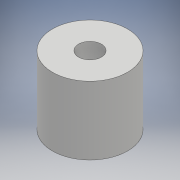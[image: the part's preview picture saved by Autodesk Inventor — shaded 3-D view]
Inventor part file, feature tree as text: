
AUTODESK INVENTOR PART (.ipt)
format: ipt  version: 2018 (Build 220112000, 112)  size: 97,792 bytes
history: native  units: mm
features: extrude x1, sketch x1
ambient origin geometry x8: Origin, YZ Plane, XZ Plane, XY Plane, X Axis, Y Axis, Z Axis, Center Point
bodies: Solid1 (feature_tree)
feature tree (2):
  extrude  "Extrusion1"  Depth=30.0mm TaperAngle=0.0deg
  sketch  "Sketch1"  dims[d0=10.0mm d2=30.0mm d3=0.0mm d16=33.0mm]
